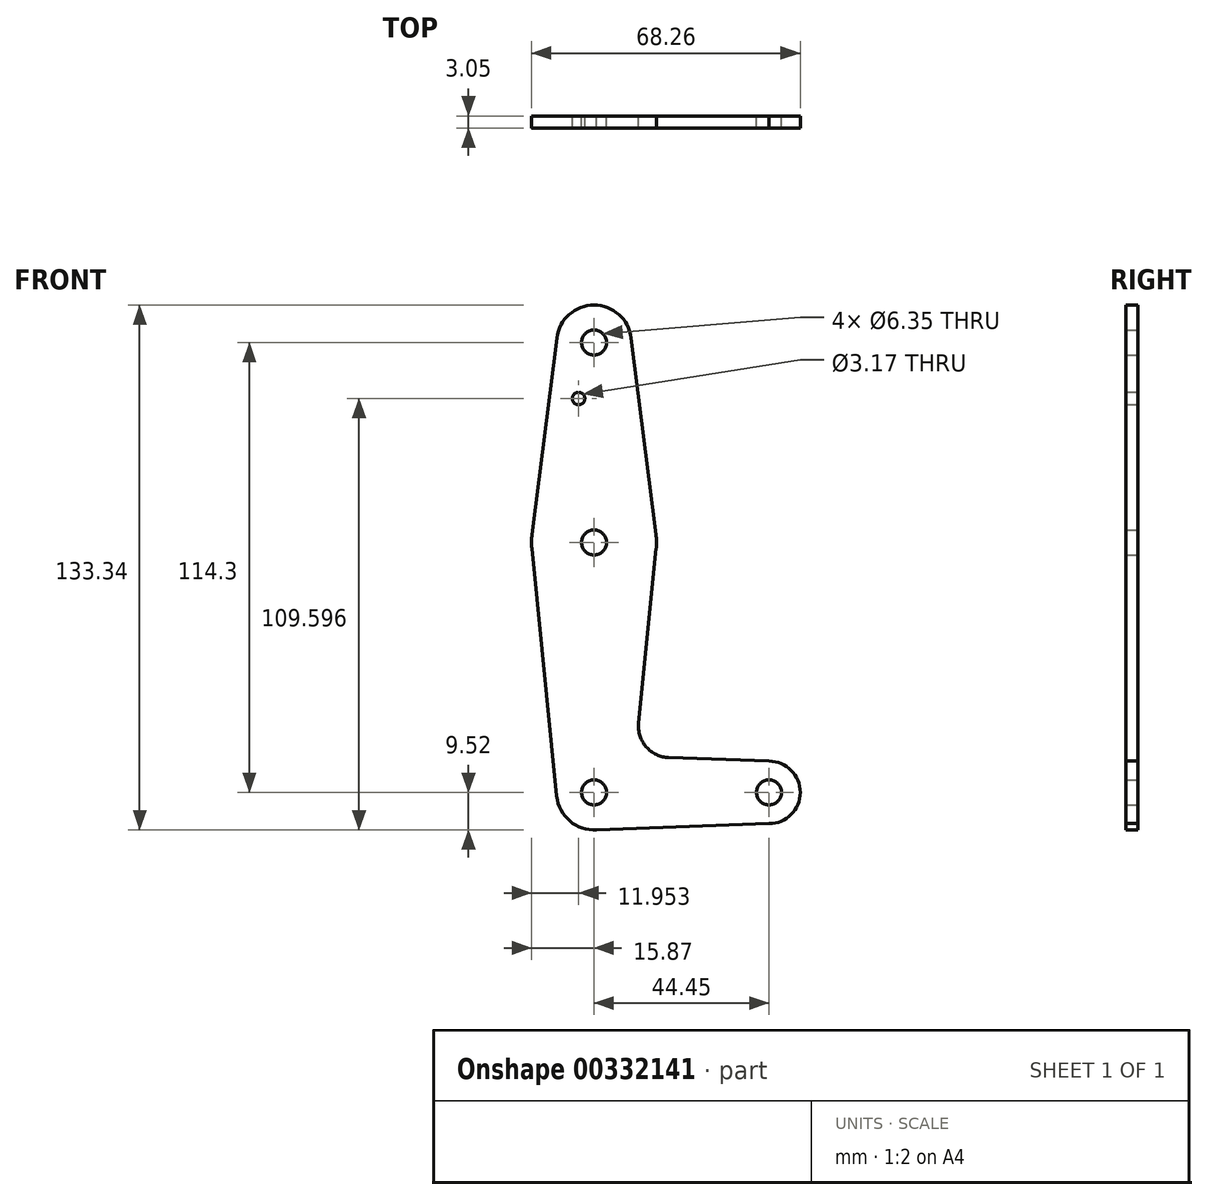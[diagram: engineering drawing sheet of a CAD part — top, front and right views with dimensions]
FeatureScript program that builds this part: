
annotation { "Feature Type Name" : "Feature", "Feature Type Description" : "" }
export const myFeature = defineFeature(function(context is Context, id is Id, definition is map)
    precondition{}
    {
        {
            var Q0;
            Q0=qCreatedBy(makeId("Front.planeOp"),FACE);
            var sketch = newSketch(context, id + "F0", { "sketchPlane" : qUnion([Q0])});
            skCircle(sketch, "E0", {"center": v(0, 0) * mm, "radius": 15.88 * mm});
            skLineSegment(sketch, "E1", {"start": v(0, 0) * mm, "end": v(0, 50.8) * mm, "construction": true});
            skCircle(sketch, "E2", {"center": v(0, 50.8) * mm, "radius": 9.53 * mm});
            skLineSegment(sketch, "E3", {"start": v(0, 0) * mm, "end": v(0, -63.5) * mm, "construction": true});
            skCircle(sketch, "E4", {"center": v(0, -63.5) * mm, "radius": 9.53 * mm});
            skLineSegment(sketch, "E5", {"start": v(0, -63.5) * mm, "end": v(44.45, -63.5) * mm, "construction": true});
            skCircle(sketch, "E6", {"center": v(44.45, -63.5) * mm, "radius": 7.94 * mm});
            skLineSegment(sketch, "E7", {"start": v(9.45, 52) * mm, "end": v(15.75, 1.98) * mm});
            skLineSegment(sketch, "E8", {"start": v(-9.45, 52) * mm, "end": v(-15.75, 1.98) * mm});
            skLineSegment(sketch, "E9", {"start": v(15.8, -1.59) * mm, "end": v(11.34, -45.91) * mm});
            skLineSegment(sketch, "E10", {"start": v(-15.8, -1.59) * mm, "end": v(-9.48, -64.45) * mm});
            skLineSegment(sketch, "E11", {"start": v(18.97, -54.65) * mm, "end": v(44.45, -55.56) * mm});
            skLineSegment(sketch, "E12", {"start": v(0, -73.02) * mm, "end": v(44.45, -71.44) * mm});
            skCircle(sketch, "E13", {"center": v(0, 50.8) * mm, "radius": 3.18 * mm});
            skCircle(sketch, "E14", {"center": v(-3.92, 36.58) * mm, "radius": 1.59 * mm});
            skCircle(sketch, "E15", {"center": v(0, 0) * mm, "radius": 3.18 * mm});
            skCircle(sketch, "E16", {"center": v(0, -63.5) * mm, "radius": 3.18 * mm});
            skCircle(sketch, "E17", {"center": v(44.45, -63.5) * mm, "radius": 3.18 * mm});
            skArc(sketch, "E18.filletArc", {"start": v(11.34, -45.91) * mm, "mid": v(13.26, -51.93) * mm, "end": v(18.97, -54.65) * mm});
            skSolve(sketch);
        }
        {
            var Q0;
            Q0 = qSketchRegion(id + "F0", true);
            extrude(context, id + "F1", {"entities" : qUnion([Q0]), "depth" : 3.05 * mm});
        }
    });
